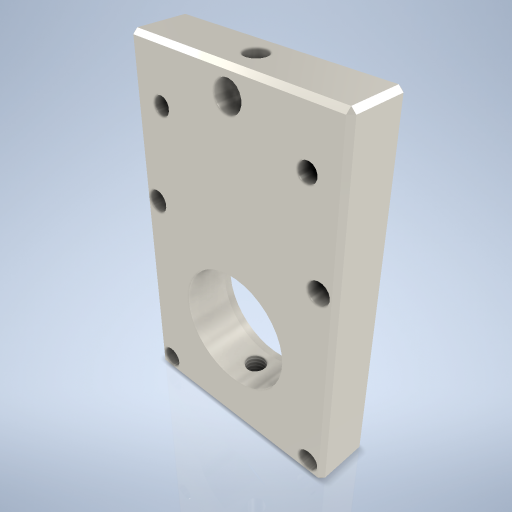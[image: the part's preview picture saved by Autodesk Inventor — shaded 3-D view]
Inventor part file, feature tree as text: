
AUTODESK INVENTOR PART (.ipt)
format: ipt  version: 2024.2 (Build 282272000, 272)  size: 340,480 bytes
history: native  units: mm
features: sketch x7, hole x6, extrude x1, chamfer x1
ambient origin geometry x8: Origin, YZ Plane, XZ Plane, XY Plane, X Axis, Y Axis, Z Axis, Center Point
bodies: Volumenkörper1 (feature_tree)
feature tree (15):
  extrude  "Extrusion1"  Depth=80.0mm
  hole  "Bohrung1"  [1 undecoded]
  hole  "Bohrung2"  [1 undecoded]
  hole  "Bohrung3"  [1 undecoded]
  hole  "Bohrung4"  [1 undecoded]
  hole  "Bohrung5"  [1 undecoded]
  hole  "Bohrung6"  [1 undecoded]
  chamfer  "Fasen1"  Distance=1.0mm Angle=45.0deg
  sketch  "Skizze1"  dims[d0=50.0mm d1=80.0mm]
  sketch  "Skizze2"  dims[d2=13.0mm d3=0.0mm]
  sketch  "Skizze3"  dims[d4=27.0mm d5=6.0mm d6=29.0mm d7=2.5mm d8=90.0deg d9=5.0mm d10=0.0mm d11=25.0mm]
  sketch  "Skizze4"  dims[d12=5.0mm d13=6.0mm d14=29.0mm d15=2.0mm d16=90.0deg d17=8.0mm d18=0.0mm d19=42.248mm]
  sketch  "Skizze5"  dims[d21=42.248mm]
  sketch  "Skizze6"  dims[d23=6.5mm d24=6.0mm d25=4.0mm d26=2.0mm d27=90.0deg d28=8.0mm d29=0.0mm]
  sketch  "Skizze7"  dims[d30=4.134mm d31=10.0mm d32=4.0mm d33=2.0mm d34=90.0deg d35=8.0mm d36=0.0mm d39=35.0mm d40=17.5mm d41=4.917mm d42=12.0mm d43=29.0mm d44=2.5mm d45=90.0deg d46=8.0mm d47=0.0mm d48=4.134mm d49=10.0mm d50=4.0mm d51=2.0mm d52=90.0deg d53=14.0mm d54=0.0mm d55=19.0mm d56=19.0mm d57=1.0mm d58=2.0mm d59=45.0deg d60=12.5mm d61=25.0mm]
note: 6 required parameter values undecoded (feature->parameter linkage not recoverable at this tier; creation-order binding heuristic only, values carry confidence <= 0.55)
